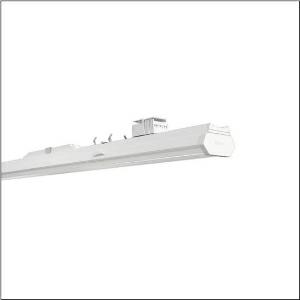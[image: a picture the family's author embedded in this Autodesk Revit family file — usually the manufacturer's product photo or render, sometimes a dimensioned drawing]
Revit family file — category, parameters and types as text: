
# Revit family: licross_r__11_protected_mo_51tp12dn495g_6914
name_source: partatom
category: Lighting Fixtures
units: mm (PartAtom-declared; Revit-internal decimal feet)

## family parameters
Cut with Voids When Loaded = No
Host = Face
Light Source = No
Part Type = Normal
Room Calculation Point = No
Round Connector Dimension = Use Diameter
Shared = No

## types (1)
- --- (1 x LED, 9980 lm, 57.1 W, 4000K)
    Apparent Load = 57 VA
    CIE Flux Codes = 73 92 98 99 100
    Color Rendering = 80
    Color Temperature = 4000K
    Default Elevation = 1800 mm
    Description = Licross® 11 Protected MO, luminaire insert, of sheet steel, galvanised, coil coated, white, length: 1.500mm, width: 90mm, height: 101mm, LED rated luminous flux: 9.980lm, light colour: 840, control gear: DALI 2, with plug, 5-pole, with phase selection, mains connection: 220..240V, AC, 50/60Hz, rated input power: 57W, internal wiring halogen-free, primary optical cover: cover, of PMMA, light emission: direct distribution, primary light characteristic: symmetric, protection rating (complete): IP64, insulation class (complete): insulation class I (protective earthing), certification: CE, ENEC, VDE, UKCA, protection symbol: D if used in an environment with conductive dust loads with corresponding accessories, impact resistance: IK06, permissible ambient temperature for indoor applications: -25..+35°C, corresponds to IFS (International Featured Standards) requirements for safety and quality in the food industry, reducing of maximum allowable ambient temperature of 5°C with ceiling mounting, LABS conformity tested according to VDMA 24364:2018-05, packaging unit: 1 piece
    Height = 92 mm
    Lamp = 1 x LED
    Lamp Light Flux = 9980 lm
    Lamp Power = 57.1 W
    Lamp count = 1
    Length = 1500 mm
    Luminous efficacy = 175 lm/W
    Manufacturer = Siteco
    ModVariant = No
    Model = 51TP12DN495G
    Mounting Place = Ceiling
    Mounting Type = Pendant
    Number of Poles = 1
    OnlyDefault = Yes
    Power Factor = 1
    Product Name = Licross® 11 Protected MO
    Product group = luminaire insert | ceiling pendant
    ProductGroupID = 902
    Protection Class = Protection class I
    Protection Degree = IP 64
    RLX_Detail_Level = 1
    RLX_Emergency_Light_Flux = 0 lm
    RLX_Emergency_Type = 0
    RLX_Emergency_Type_DB = No
    RlxData = <blob elided: 24517 chars, md5=096e8973>
    Socket = socket
    Standby Power = 0 W
    System Light Flux = 9980 lm
    System Power = 57 W
    Type Comments = factory setting: luminous flux: 100 % | dim-lin: 254 | 378 mA
    Type Image = l_1256148.jpg
    URL = http://relux.com
    VarID = @adj_122533
    Voltage = 0 V
    Weight = 0.00 kg
    Width = 88 mm

## geometry (parser evidence)
native form markers: Blend x4, Sweep x11
no freeform markers — native parametric forms only
